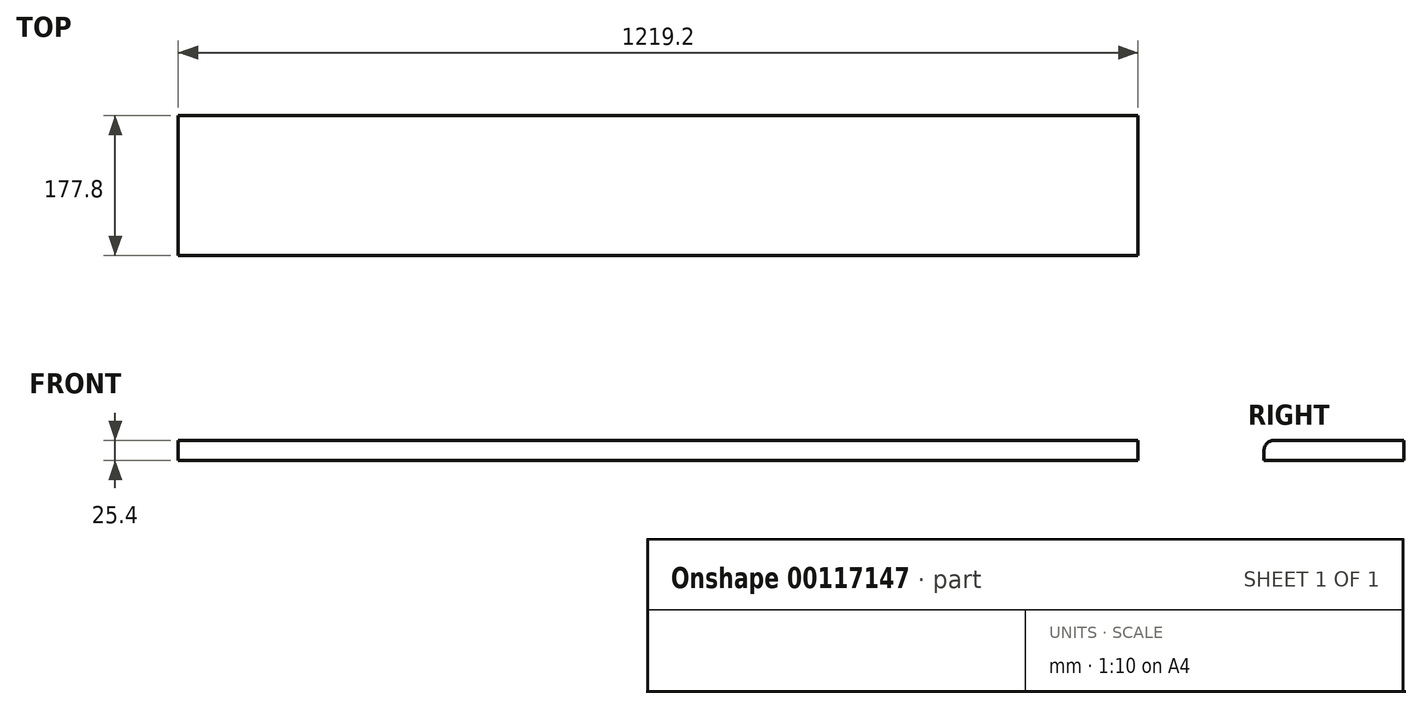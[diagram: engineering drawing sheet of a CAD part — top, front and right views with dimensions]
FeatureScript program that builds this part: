
annotation { "Feature Type Name" : "Feature", "Feature Type Description" : "" }
export const myFeature = defineFeature(function(context is Context, id is Id, definition is map)
    precondition{}
    {
        {
            var Q0;
            Q0=qCreatedBy(makeId("Top.planeOp"),FACE);
            var sketch = newSketch(context, id + "F0", { "sketchPlane" : qUnion([Q0])});
            skLineSegment(sketch, "E0.bottom", {"start": v(-588.2, 135.47) * mm, "end": v(631, 135.47) * mm});
            skLineSegment(sketch, "E0.top", {"start": v(-588.2, -42.33) * mm, "end": v(631, -42.33) * mm});
            skLineSegment(sketch, "E0.left", {"start": v(-588.2, 135.47) * mm, "end": v(-588.2, -42.33) * mm});
            skLineSegment(sketch, "E0.right", {"start": v(631, 135.47) * mm, "end": v(631, -42.33) * mm});
            skSolve(sketch);
        }
        {
            var Q0;
            Q0 = qSketchRegion(id + "F0", true);
            extrude(context, id + "F1", {"entities" : qUnion([Q0]), "depth" : 25.4 * mm});
        }
        {
            var Q0;
            Q0=makeQuery(id+"F1.opExtrude","CAP_EDGE",EDGE,{"disambiguationData":[OSD([sQuery(id+"F0.wireOp",EDGE,"E0.top")])],"isStart":false});
            fillet(context, id + "F2", {"entities" : qUnion([Q0]), "radius" : 12.7 * mm, "tangentPropagation" : true, "allowEdgeOverflow" : false});
        }
    });
